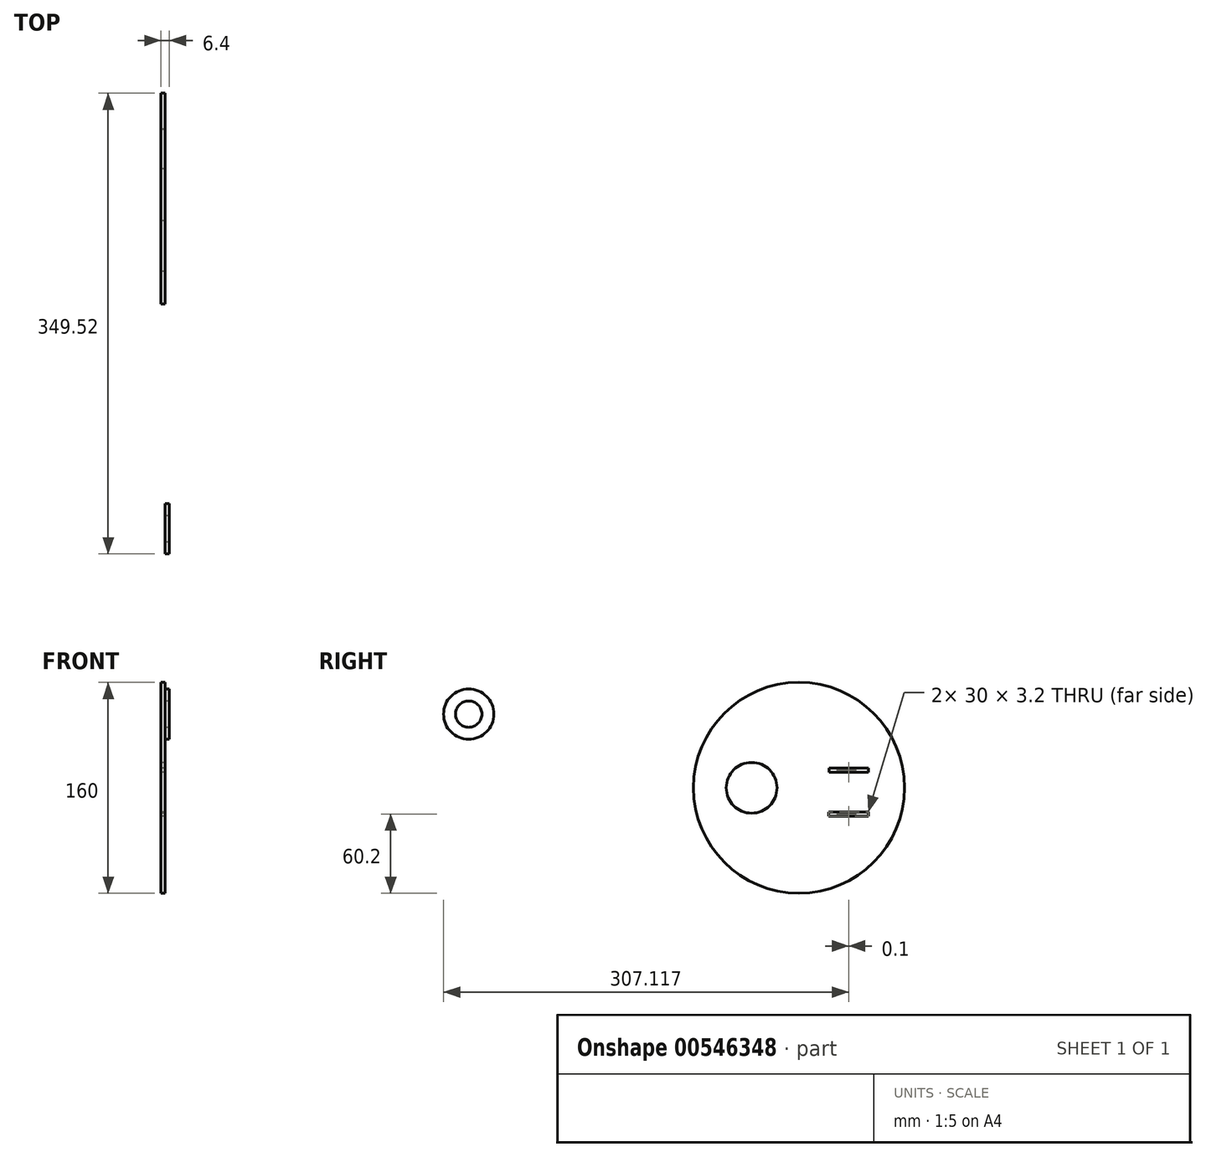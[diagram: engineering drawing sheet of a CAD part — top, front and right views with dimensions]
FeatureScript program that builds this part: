
annotation { "Feature Type Name" : "Feature", "Feature Type Description" : "" }
export const myFeature = defineFeature(function(context is Context, id is Id, definition is map)
    precondition{}
    {
        {
            var Q0;
            Q0=qCreatedBy(makeId("Right.planeOp"),FACE);
            var sketch = newSketch(context, id + "F0", { "sketchPlane" : qUnion([Q0])});
            skCircle(sketch, "E0", {"center": v(0, 0) * mm, "radius": 80 * mm});
            skLineSegment(sketch, "E1.bottom", {"start": v(22.7, 15) * mm, "end": v(52.7, 15) * mm});
            skLineSegment(sketch, "E1.top", {"start": v(22.7, 11.8) * mm, "end": v(52.7, 11.8) * mm});
            skLineSegment(sketch, "E1.left", {"start": v(22.7, 15) * mm, "end": v(22.7, 11.8) * mm});
            skLineSegment(sketch, "E1.right", {"start": v(52.7, 15) * mm, "end": v(52.7, 11.8) * mm});
            skLineSegment(sketch, "E2.bottom", {"start": v(22.6, -18.2) * mm, "end": v(52.6, -18.2) * mm});
            skLineSegment(sketch, "E2.top", {"start": v(22.6, -21.4) * mm, "end": v(52.6, -21.4) * mm});
            skLineSegment(sketch, "E2.left", {"start": v(22.6, -18.2) * mm, "end": v(22.6, -21.4) * mm});
            skLineSegment(sketch, "E2.right", {"start": v(52.6, -18.2) * mm, "end": v(52.6, -21.4) * mm});
            skCircle(sketch, "E3", {"center": v(-35.92, 0) * mm, "radius": 19.25 * mm});
            skLineSegment(sketch, "E4", {"start": v(52.7, 11.8) * mm, "end": v(52.7, 11.8) * mm});
            skSolve(sketch);
        }
        {
            var Q0;
            Q0=makeQuery(id+"F0.imprint","IMPRINT",FACE,{"disambiguationData":[TD([[makeQuery(id+"F0.imprint","IMPRINT",EDGE,{"derivedFrom":sQuery(id+"F0.wireOp",EDGE,"E0")}),1.0]])]});
            extrude(context, id + "F1", {"entities" : qUnion([Q0]), "depth" : 3.2 * mm, "offsetDistance" : 25 * mm});
        }
        {
            var Q0;
            Q0=makeQuery(id+"F1.opExtrude","CAP_FACE",FACE,{"disambiguationData":[OSD([sQuery(id+"F0.wireOp",EDGE,"E0"),sQuery(id+"F0.wireOp",EDGE,"E1.bottom"),sQuery(id+"F0.wireOp",EDGE,"E1.top"),sQuery(id+"F0.wireOp",EDGE,"E1.left"),sQuery(id+"F0.wireOp",EDGE,"E1.right"),sQuery(id+"F0.wireOp",EDGE,"E2.bottom"),sQuery(id+"F0.wireOp",EDGE,"E2.top"),sQuery(id+"F0.wireOp",EDGE,"E2.left"),sQuery(id+"F0.wireOp",EDGE,"E2.right"),sQuery(id+"F0.wireOp",EDGE,"E3")])],"isStart":false});
            var sketch = newSketch(context, id + "F2", { "sketchPlane" : qUnion([Q0])});
            skCircle(sketch, "E5", {"center": v(-250.47, 55.92) * mm, "radius": 19.05 * mm});
            skCircle(sketch, "E6", {"center": v(-250.47, 55.92) * mm, "radius": 10 * mm});
            skSolve(sketch);
        }
        {
            var Q0;
            Q0 = qSketchRegion(id + "F2", true);
            extrude(context, id + "F3", {"entities" : qUnion([Q0]), "depth" : 3.2 * mm, "offsetDistance" : 25 * mm});
        }
    });
